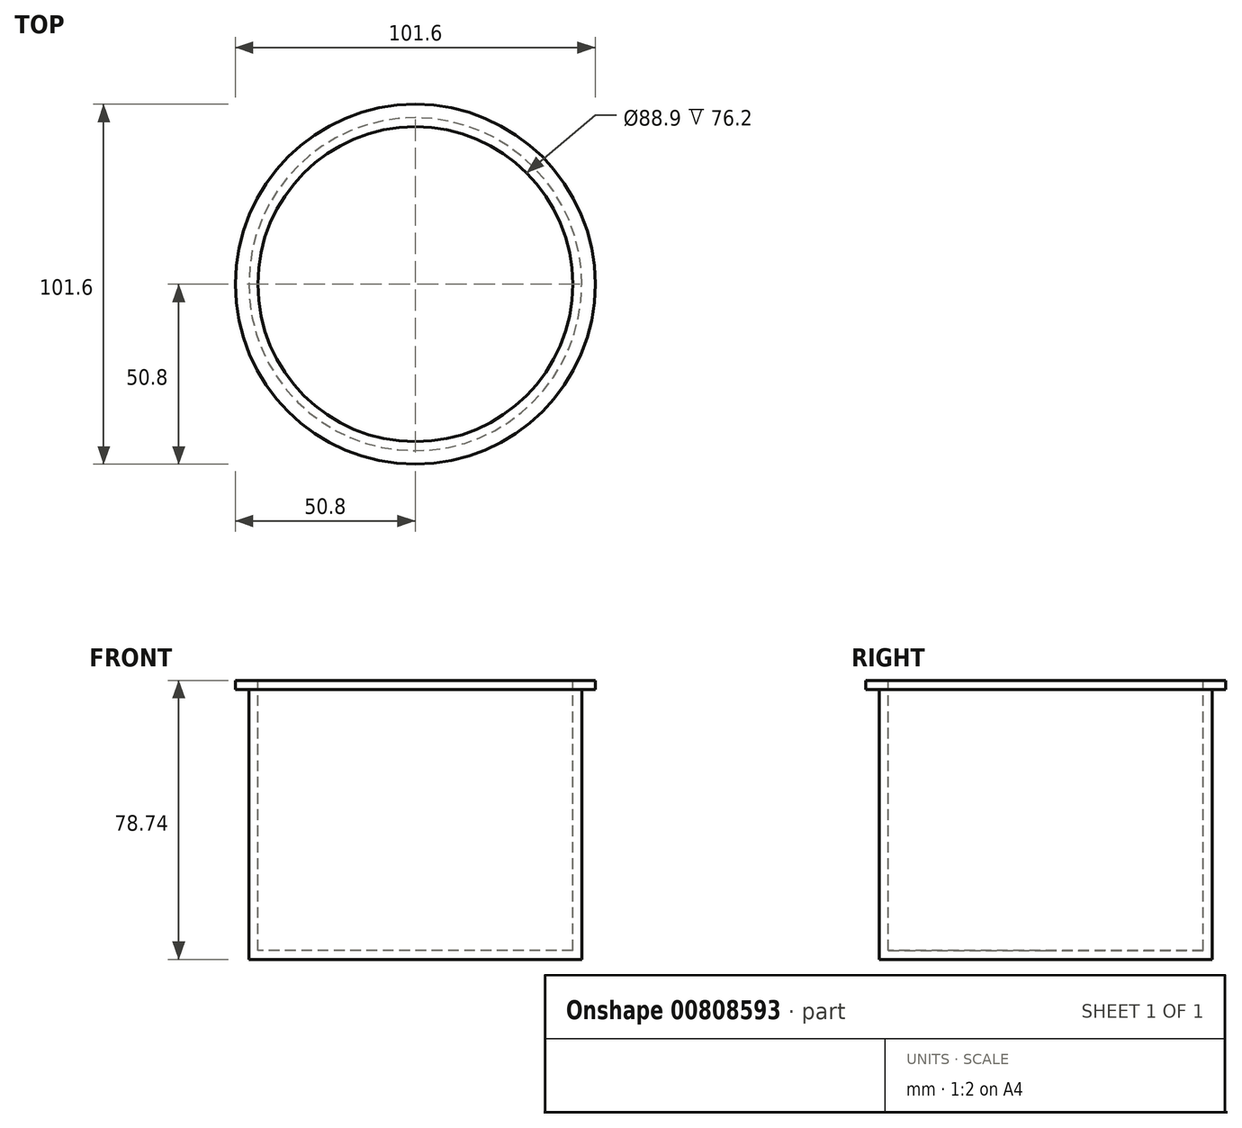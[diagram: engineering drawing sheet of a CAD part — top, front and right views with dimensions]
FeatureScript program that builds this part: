
annotation { "Feature Type Name" : "Feature", "Feature Type Description" : "" }
export const myFeature = defineFeature(function(context is Context, id is Id, definition is map)
    precondition{}
    {
        {
            var Q0;
            Q0=qCreatedBy(makeId("Top.planeOp"),FACE);
            var sketch = newSketch(context, id + "F0", { "sketchPlane" : qUnion([Q0])});
            skCircle(sketch, "E0", {"center": v(0, 0) * mm, "radius": 47 * mm});
            skSolve(sketch);
        }
        {
            var Q0;
            Q0=qCreatedBy(makeId("Top.planeOp"),FACE);
            cPlane(context, id + "F1", {"entities" : qUnion([Q0]), "cplaneType" : CPlaneType.OFFSET, "offset" : 76.2 * mm, "width" : 152.4 * mm, "height" : 152.4 * mm});
        }
        {
            var Q0;
            Q0=qCreatedBy(id+"F1.planeOp",FACE);
            var sketch = newSketch(context, id + "F2", { "sketchPlane" : qUnion([Q0])});
            skCircle(sketch, "E1", {"center": v(0, 0) * mm, "radius": 47 * mm});
            skCircle(sketch, "E2", {"center": v(0, 0) * mm, "radius": 50.8 * mm});
            skSolve(sketch);
        }
        {
            var Q0;
            Q0=makeQuery(id+"F0.imprint","IMPRINT",FACE,{"disambiguationData":[TD([[makeQuery(id+"F0.imprint","IMPRINT",EDGE,{"derivedFrom":sQuery(id+"F0.wireOp",EDGE,"E0")}),1.0]])]});
            var Q1;
            Q1=makeQuery(id+"F2.imprint","IMPRINT",FACE,{"disambiguationData":[TD([[makeQuery(id+"F2.imprint","IMPRINT",EDGE,{"derivedFrom":sQuery(id+"F2.wireOp",EDGE,"E1")}),1.0]])]});
            loft(context, id + "F3", {"sheetProfilesArray" : [{ "sheetProfileEntities" : qUnion([Q0]) }, { "sheetProfileEntities" : qUnion([Q1]) }]});
        }
        {
            var Q0;
            Q0=makeQuery(id+"F3.opLoft","CAP_FACE",FACE,{"disambiguationData":[OSD([makeQuery(id+"F2.imprint","IMPRINT",FACE,{"disambiguationData":[TD([[makeQuery(id+"F2.imprint","IMPRINT",EDGE,{"derivedFrom":sQuery(id+"F2.wireOp",EDGE,"E1")}),1.0]])]})])],"isStart":true});
            shell(context, id + "F4", {"entities" : qUnion([Q0]), "thickness" : 2.54 * mm});
        }
        {
            var Q0;
            Q0=qCreatedBy(makeId("Top.planeOp"),FACE);
            cPlane(context, id + "F5", {"entities" : qUnion([Q0]), "cplaneType" : CPlaneType.OFFSET, "offset" : 78.74 * mm, "width" : 152.4 * mm, "height" : 152.4 * mm});
        }
        {
            var Q0;
            Q0=qCreatedBy(id+"F5.planeOp",FACE);
            var sketch = newSketch(context, id + "F6", { "sketchPlane" : qUnion([Q0])});
            skCircle(sketch, "E3", {"center": v(0, 0) * mm, "radius": 50.8 * mm});
            skCircle(sketch, "E4.0", {"center": v(0, 0) * mm, "radius": 44.45 * mm});
            skSolve(sketch);
        }
        {
            var Q0;
            Q0=makeQuery(id+"F6.imprint","IMPRINT",FACE,{"disambiguationData":[TD([[makeQuery(id+"F6.imprint","IMPRINT",EDGE,{"derivedFrom":sQuery(id+"F6.wireOp",EDGE,"E3")}),1.0]])]});
            extrude(context, id + "F7", {"entities" : qUnion([Q0]), "operationType" : NewBodyOperationType.ADD, "oppositeDirection" : true, "depth" : 2.54 * mm, "offsetDistance" : 25.4 * mm});
        }
    });
